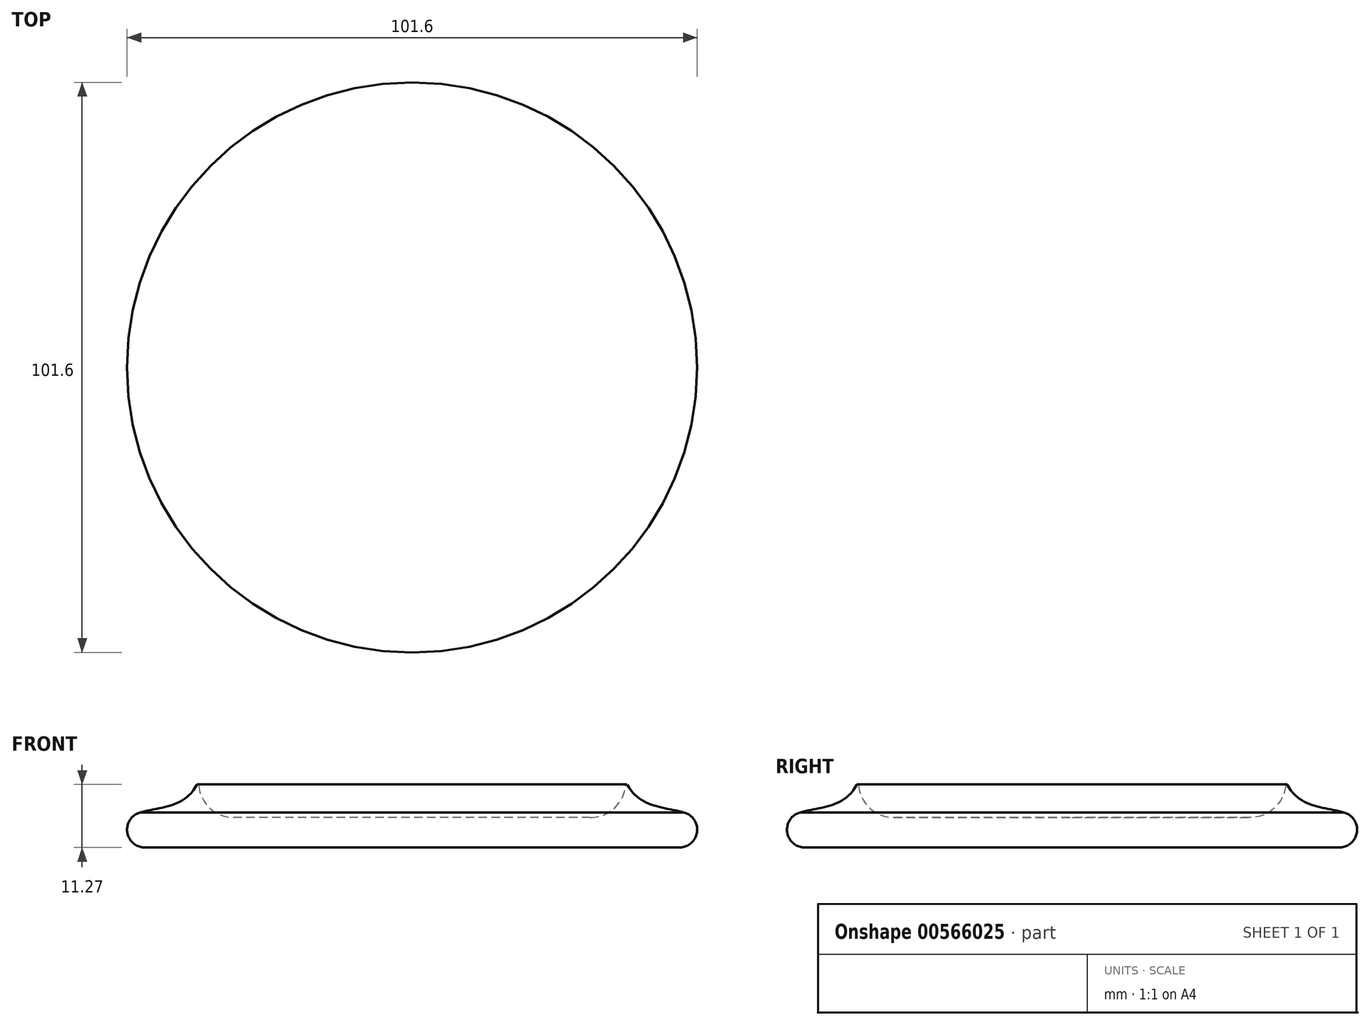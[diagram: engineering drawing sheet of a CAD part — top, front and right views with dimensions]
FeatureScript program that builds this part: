
annotation { "Feature Type Name" : "Feature", "Feature Type Description" : "" }
export const myFeature = defineFeature(function(context is Context, id is Id, definition is map)
    precondition{}
    {
        {
            var Q0;
            Q0=qCreatedBy(makeId("Top.planeOp"),FACE);
            var sketch = newSketch(context, id + "F0", { "sketchPlane" : qUnion([Q0])});
            skCircle(sketch, "E0", {"center": v(0, 0) * mm, "radius": 50.8 * mm});
            skSolve(sketch);
        }
        {
            var Q0;
            Q0=qCreatedBy(makeId("Front.planeOp"),FACE);
            var sketch = newSketch(context, id + "F1", { "sketchPlane" : qUnion([Q0])});
            skLineSegment(sketch, "E1", {"start": v(38.1, 6.35) * mm, "end": v(38.1, 6.35) * mm});
            skLineSegment(sketch, "E2", {"start": v(31.75, 0) * mm, "end": v(0, 0) * mm});
            skLineSegment(sketch, "E3", {"start": v(0, 0) * mm, "end": v(0, -5.37) * mm});
            skLineSegment(sketch, "E4", {"start": v(0, -5.37) * mm, "end": v(47.62, -5.37) * mm});
            skLineSegment(sketch, "E5", {"start": v(50.8, -2.2) * mm, "end": v(50.8, -2.18) * mm});
            skFitSpline(sketch, "E6", {"points": [v(50.8, 0) * mm, v(38.1, 6.35) * mm], "startDerivative": vector(-12.9, 6.74) * mm, "endDerivative": vector(-7.44, 16.69) * mm});
            skPoint(sketch, "E7.visualSharp", {"position": v(38.1, 0) * mm});
            skArc(sketch, "E7.filletArc", {"start": v(31.75, 0) * mm, "mid": v(36.02, 1.65) * mm, "end": v(38.07, 5.73) * mm});
            skPoint(sketch, "E8.visualSharp", {"position": v(50.8, -5.37) * mm});
            skArc(sketch, "E8.filletArc", {"start": v(47.62, -5.37) * mm, "mid": v(49.87, -4.44) * mm, "end": v(50.8, -2.2) * mm});
            skArc(sketch, "E9.filletArc", {"start": v(50.8, -2.18) * mm, "mid": v(50.15, -0.25) * mm, "end": v(48.46, 0.88) * mm});
            skPoint(sketch, "E10.visualSharp", {"position": v(38.24, 6.05) * mm});
            skPoint(sketch, "E11.visualSharp", {"position": v(38.1, 6.06) * mm});
            skArc(sketch, "E11.filletArc", {"start": v(38.08, 5.8) * mm, "mid": v(38.07, 5.76) * mm, "end": v(38.07, 5.73) * mm});
            skPoint(sketch, "E12.visualSharp", {"position": v(38.26, 6.01) * mm});
            skArc(sketch, "E12.filletArc", {"start": v(38.36, 5.82) * mm, "mid": v(38.2, 5.9) * mm, "end": v(38.08, 5.8) * mm});
            skSolve(sketch);
        }
        {
            var Q0;
            Q0 = qSketchRegion(id + "F1", true);
            var Q1;
            Q1=sQuery(id+"F1.wireOp",EDGE,"E3");
            revolve(context, id + "F2", {"entities" : qUnion([Q0]), "axis" : qUnion([Q1]), "revolveType" : RevolveType.FULL});
        }
    });
